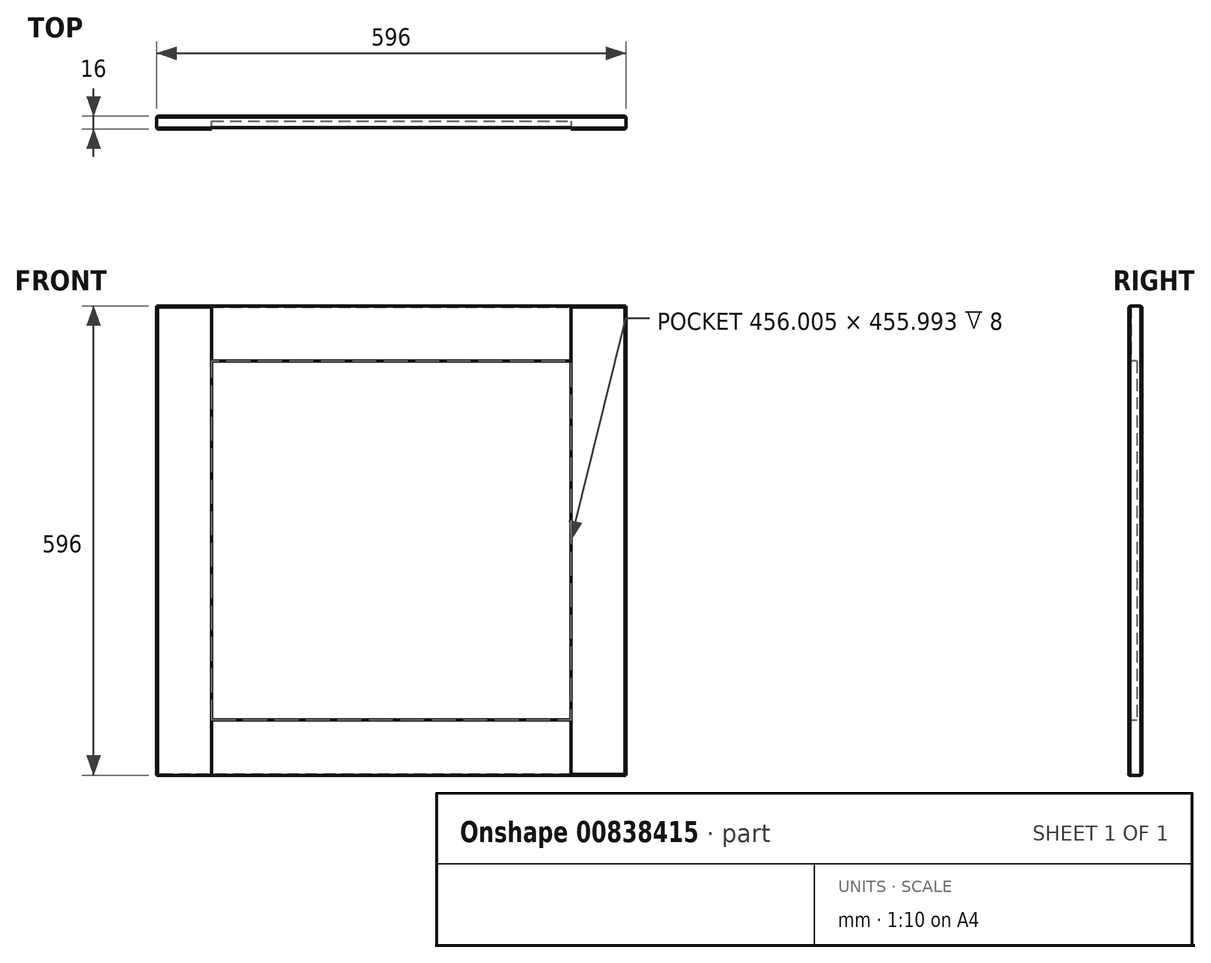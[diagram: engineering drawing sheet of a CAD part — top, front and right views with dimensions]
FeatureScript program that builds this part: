
annotation { "Feature Type Name" : "Feature", "Feature Type Description" : "" }
export const myFeature = defineFeature(function(context is Context, id is Id, definition is map)
    precondition{}
    {
        {
            var Q0;
            Q0=qCreatedBy(makeId("Front.planeOp"),FACE);
            var sketch = newSketch(context, id + "F0", { "sketchPlane" : qUnion([Q0])});
            skLineSegment(sketch, "E0.bottom", {"start": v(0, 0) * mm, "end": v(35.9, 0) * mm});
            skLineSegment(sketch, "E0.top", {"start": v(0, 30.12) * mm, "end": v(35.9, 30.12) * mm});
            skLineSegment(sketch, "E0.left", {"start": v(0, 0) * mm, "end": v(0, 30.12) * mm});
            skLineSegment(sketch, "E0.right", {"start": v(35.9, 0) * mm, "end": v(35.9, 30.12) * mm});
            skSolve(sketch);
        }
        {
            var Q0;
            Q0=makeQuery(id+"F0.imprint","IMPRINT",FACE,{"disambiguationData":[TD([[makeQuery(id+"F0.imprint","IMPRINT",EDGE,{"derivedFrom":sQuery(id+"F0.wireOp",EDGE,"E0.bottom")}),1.0]])]});
            extrude(context, id + "F1", {"entities" : qUnion([Q0]), "depth" : 16 * mm, "offsetDistance" : 25.4 * mm});
        }
        {
            var Q0;
            Q0=makeQuery(id+"F1.opExtrude","SWEPT_FACE",FACE,{"disambiguationData":[OSD([sQuery(id+"F0.wireOp",EDGE,"E0.left")])]});
            extrude(context, id + "F2", {"entities" : qUnion([Q0]), "operationType" : NewBodyOperationType.ADD, "oppositeDirection" : true, "depth" : 196 * mm, "offsetDistance" : 25 * mm});
        }
        {
            var Q0;
            {var subQ0=sQuery(id+"F0.wireOp",EDGE,"E0.bottom");Q0=makeQuery(id+"F2.boolean.opBoolean","MERGE",FACE,{"derivedFrom":[makeQuery(id+"F1.opExtrude","SWEPT_FACE",FACE,{"disambiguationData":[OSD([subQ0])]}),makeQuery(id+"F2.opExtrude","SWEPT_FACE",FACE,{"disambiguationData":[OSD([subQ0,sQuery(id+"F0.wireOp",EDGE,"E0.left")])]})]});}
            extrude(context, id + "F3", {"entities" : qUnion([Q0]), "operationType" : NewBodyOperationType.ADD, "oppositeDirection" : true, "depth" : 796 * mm, "offsetDistance" : 25 * mm});
        }
        {
            var Q0;
            {var subQ0=sQuery(id+"F0.wireOp",EDGE,"E0.left");var subQ1=sQuery(id+"F0.wireOp",EDGE,"E0.bottom");Q0=makeQuery(id+"F3.boolean.opBoolean","MERGE",FACE,{"derivedFrom":[makeQuery(id+"F2.boolean.opBoolean","MERGE",FACE,{"derivedFrom":[makeQuery(id+"F1.opExtrude","CAP_FACE",FACE,{"disambiguationData":[OSD([subQ1,sQuery(id+"F0.wireOp",EDGE,"E0.top"),subQ0,sQuery(id+"F0.wireOp",EDGE,"E0.right")])],"isStart":false}),makeQuery(id+"F2.opExtrude","SWEPT_FACE",FACE,{"disambiguationData":[OSD([subQ0]),TDD([makeQuery(id+"F1.opExtrude","CAP_EDGE",EDGE,{"disambiguationData":[OSD([subQ0])],"isStart":false})])]})]}),makeQuery(id+"F3.opExtrude","SWEPT_FACE",FACE,{"disambiguationData":[OSD([subQ1,subQ0]),TDD([makeQuery(id+"F2.boolean.opBoolean","MERGE",EDGE,{"derivedFrom":[makeQuery(id+"F1.opExtrude","CAP_EDGE",EDGE,{"disambiguationData":[OSD([subQ1])],"isStart":false}),makeQuery(id+"F2.opExtrude","SWEPT_EDGE",EDGE,{"disambiguationData":[OSD([subQ1,subQ0]),TDD([makeQuery(id+"F1.opExtrude","CAP_VERTEX",VERTEX,{"disambiguationData":[OSD([subQ1,subQ0])],"isStart":false})])]})]})])]})]});}
            var sketch = newSketch(context, id + "F4", { "sketchPlane" : qUnion([Q0])});
            skLineSegment(sketch, "E1.bottom", {"start": v(0, 796) * mm, "end": v(42.19, 796) * mm});
            skLineSegment(sketch, "E1.top", {"start": v(0, 751.57) * mm, "end": v(42.19, 751.57) * mm});
            skLineSegment(sketch, "E1.left", {"start": v(0, 796) * mm, "end": v(0, 751.57) * mm});
            skLineSegment(sketch, "E1.right", {"start": v(42.19, 796) * mm, "end": v(42.19, 751.57) * mm});
            skLineSegment(sketch, "E2.bottom", {"start": v(196, 796) * mm, "end": v(153.6, 796) * mm});
            skLineSegment(sketch, "E2.top", {"start": v(196, 746.75) * mm, "end": v(153.6, 746.75) * mm});
            skLineSegment(sketch, "E2.left", {"start": v(196, 796) * mm, "end": v(196, 746.75) * mm});
            skLineSegment(sketch, "E2.right", {"start": v(153.6, 796) * mm, "end": v(153.6, 746.75) * mm});
            skSolve(sketch);
        }
        {
            var Q0;
            Q0=makeQuery(id+"F4.imprint","IMPRINT",FACE,{"disambiguationData":[TD([[makeQuery(id+"F4.imprint","IMPRINT",EDGE,{"derivedFrom":sQuery(id+"F4.wireOp",EDGE,"E1.bottom")}),-1.0]])]});
            var Q1;
            Q1=makeQuery(id+"F4.imprint","IMPRINT",FACE,{"disambiguationData":[TD([[makeQuery(id+"F4.imprint","IMPRINT",EDGE,{"derivedFrom":sQuery(id+"F4.wireOp",EDGE,"E2.bottom")}),-1.0]])]});
            extrude(context, id + "F5", {"entities" : qUnion([Q0, Q1]), "operationType" : NewBodyOperationType.ADD, "depth" : 25 * mm, "offsetDistance" : 25 * mm});
        }
        {
            var Q0;
            {var subQ0=sQuery(id+"F0.wireOp",EDGE,"E0.left");var subQ1=sQuery(id+"F0.wireOp",EDGE,"E0.bottom");Q0=makeQuery(id+"F3.boolean.opBoolean","MERGE",FACE,{"derivedFrom":[makeQuery(id+"F2.boolean.opBoolean","MERGE",FACE,{"derivedFrom":[makeQuery(id+"F1.opExtrude","CAP_FACE",FACE,{"disambiguationData":[OSD([subQ1,sQuery(id+"F0.wireOp",EDGE,"E0.top"),subQ0,sQuery(id+"F0.wireOp",EDGE,"E0.right")])],"isStart":false}),makeQuery(id+"F2.opExtrude","SWEPT_FACE",FACE,{"disambiguationData":[OSD([subQ0]),TDD([makeQuery(id+"F1.opExtrude","CAP_EDGE",EDGE,{"disambiguationData":[OSD([subQ0])],"isStart":false})])]})]}),makeQuery(id+"F3.opExtrude","SWEPT_FACE",FACE,{"disambiguationData":[OSD([subQ1,subQ0]),TDD([makeQuery(id+"F2.boolean.opBoolean","MERGE",EDGE,{"derivedFrom":[makeQuery(id+"F1.opExtrude","CAP_EDGE",EDGE,{"disambiguationData":[OSD([subQ1])],"isStart":false}),makeQuery(id+"F2.opExtrude","SWEPT_EDGE",EDGE,{"disambiguationData":[OSD([subQ1,subQ0]),TDD([makeQuery(id+"F1.opExtrude","CAP_VERTEX",VERTEX,{"disambiguationData":[OSD([subQ1,subQ0])],"isStart":false})])]})]})])]})]});}
            var sketch = newSketch(context, id + "F6", { "sketchPlane" : qUnion([Q0])});
            skLineSegment(sketch, "E3.bottom", {"start": v(196, 0) * mm, "end": v(163.38, 0) * mm});
            skLineSegment(sketch, "E3.top", {"start": v(196, 46.55) * mm, "end": v(163.38, 46.55) * mm});
            skLineSegment(sketch, "E3.left", {"start": v(196, 0) * mm, "end": v(196, 46.55) * mm});
            skLineSegment(sketch, "E3.right", {"start": v(163.38, 0) * mm, "end": v(163.38, 46.55) * mm});
            skLineSegment(sketch, "E4.bottom", {"start": v(0, 0) * mm, "end": v(50.28, 0) * mm});
            skLineSegment(sketch, "E4.top", {"start": v(0, 44.4) * mm, "end": v(50.28, 44.4) * mm});
            skLineSegment(sketch, "E4.left", {"start": v(0, 0) * mm, "end": v(0, 44.4) * mm});
            skLineSegment(sketch, "E4.right", {"start": v(50.28, 0) * mm, "end": v(50.28, 44.4) * mm});
            skSolve(sketch);
        }
        {
            var Q0;
            Q0=makeQuery(id+"F6.imprint","IMPRINT",FACE,{"disambiguationData":[TD([[makeQuery(id+"F6.imprint","IMPRINT",EDGE,{"derivedFrom":sQuery(id+"F6.wireOp",EDGE,"E3.bottom")}),1.0]])]});
            var Q1;
            Q1=makeQuery(id+"F6.imprint","IMPRINT",FACE,{"disambiguationData":[TD([[makeQuery(id+"F6.imprint","IMPRINT",EDGE,{"derivedFrom":sQuery(id+"F6.wireOp",EDGE,"E4.bottom")}),1.0]])]});
            extrude(context, id + "F7", {"entities" : qUnion([Q0, Q1]), "operationType" : NewBodyOperationType.ADD, "depth" : 25 * mm, "offsetDistance" : 25 * mm});
        }
        {
            var Q0;
            Q0=makeQuery(id+"F7.opExtrude","SWEPT_FACE",FACE,{"disambiguationData":[OSD([sQuery(id+"F6.wireOp",EDGE,"E4.right")])]});
            extrude(context, id + "F8", {"entities" : qUnion([Q0]), "operationType" : NewBodyOperationType.ADD, "depth" : 19.72 * mm, "offsetDistance" : 25 * mm});
        }
        {
            var Q0;
            {var subQ0=sQuery(id+"F6.wireOp",EDGE,"E4.top");Q0=makeQuery(id+"F8.boolean.opBoolean","MERGE",FACE,{"derivedFrom":[makeQuery(id+"F7.opExtrude","SWEPT_FACE",FACE,{"disambiguationData":[OSD([subQ0])]}),makeQuery(id+"F8.opExtrude","SWEPT_FACE",FACE,{"disambiguationData":[OSD([subQ0,sQuery(id+"F6.wireOp",EDGE,"E4.right")])]})]});}
            extrude(context, id + "F9", {"entities" : qUnion([Q0]), "operationType" : NewBodyOperationType.ADD, "depth" : 25.6 * mm, "offsetDistance" : 25 * mm});
        }
        {
            var Q0;
            Q0=makeQuery(id+"F7.opExtrude","SWEPT_FACE",FACE,{"disambiguationData":[OSD([sQuery(id+"F6.wireOp",EDGE,"E3.right")])]});
            extrude(context, id + "F10", {"entities" : qUnion([Q0]), "operationType" : NewBodyOperationType.ADD, "depth" : 37.38 * mm, "offsetDistance" : 25 * mm});
        }
        {
            var Q0;
            {var subQ0=sQuery(id+"F6.wireOp",EDGE,"E3.top");Q0=makeQuery(id+"F10.boolean.opBoolean","MERGE",FACE,{"derivedFrom":[makeQuery(id+"F7.opExtrude","SWEPT_FACE",FACE,{"disambiguationData":[OSD([subQ0])]}),makeQuery(id+"F10.opExtrude","SWEPT_FACE",FACE,{"disambiguationData":[OSD([subQ0,sQuery(id+"F6.wireOp",EDGE,"E3.right")])]})]});}
            extrude(context, id + "F11", {"entities" : qUnion([Q0]), "operationType" : NewBodyOperationType.ADD, "depth" : 23.45 * mm, "offsetDistance" : 25 * mm});
        }
        {
            var Q0;
            Q0=makeQuery(id+"F5.opExtrude","SWEPT_FACE",FACE,{"disambiguationData":[OSD([sQuery(id+"F4.wireOp",EDGE,"E1.right")])]});
            extrude(context, id + "F12", {"entities" : qUnion([Q0]), "operationType" : NewBodyOperationType.ADD, "depth" : 27.8 * mm, "offsetDistance" : 25 * mm});
        }
        {
            var Q0;
            {var subQ0=sQuery(id+"F4.wireOp",EDGE,"E1.top");Q0=makeQuery(id+"F12.boolean.opBoolean","MERGE",FACE,{"derivedFrom":[makeQuery(id+"F5.opExtrude","SWEPT_FACE",FACE,{"disambiguationData":[OSD([subQ0])]}),makeQuery(id+"F12.opExtrude","SWEPT_FACE",FACE,{"disambiguationData":[OSD([subQ0,sQuery(id+"F4.wireOp",EDGE,"E1.right")])]})]});}
            extrude(context, id + "F13", {"entities" : qUnion([Q0]), "operationType" : NewBodyOperationType.ADD, "depth" : 25.57 * mm, "offsetDistance" : 25 * mm});
        }
        {
            var Q0;
            Q0=makeQuery(id+"F5.opExtrude","SWEPT_FACE",FACE,{"disambiguationData":[OSD([sQuery(id+"F4.wireOp",EDGE,"E2.top")])]});
            extrude(context, id + "F14", {"entities" : qUnion([Q0]), "operationType" : NewBodyOperationType.ADD, "depth" : 20.75 * mm, "offsetDistance" : 25 * mm});
        }
        {
            var Q0;
            {var subQ0=sQuery(id+"F4.wireOp",EDGE,"E2.right");Q0=makeQuery(id+"F14.boolean.opBoolean","MERGE",FACE,{"derivedFrom":[makeQuery(id+"F5.opExtrude","SWEPT_FACE",FACE,{"disambiguationData":[OSD([subQ0])]}),makeQuery(id+"F14.opExtrude","SWEPT_FACE",FACE,{"disambiguationData":[OSD([sQuery(id+"F4.wireOp",EDGE,"E2.top"),subQ0])]})]});}
            extrude(context, id + "F15", {"entities" : qUnion([Q0]), "operationType" : NewBodyOperationType.ADD, "depth" : 27.6 * mm, "offsetDistance" : 25 * mm});
        }
        {
            var Q0;
            {var subQ0=sQuery(id+"F0.wireOp",EDGE,"E0.left");var subQ1=sQuery(id+"F0.wireOp",EDGE,"E0.bottom");Q0=makeQuery(id+"F3.boolean.opBoolean","MERGE",FACE,{"derivedFrom":[makeQuery(id+"F2.boolean.opBoolean","MERGE",FACE,{"derivedFrom":[makeQuery(id+"F1.opExtrude","CAP_FACE",FACE,{"disambiguationData":[OSD([subQ1,sQuery(id+"F0.wireOp",EDGE,"E0.top"),subQ0,sQuery(id+"F0.wireOp",EDGE,"E0.right")])],"isStart":false}),makeQuery(id+"F2.opExtrude","SWEPT_FACE",FACE,{"disambiguationData":[OSD([subQ0]),TDD([makeQuery(id+"F1.opExtrude","CAP_EDGE",EDGE,{"disambiguationData":[OSD([subQ0])],"isStart":false})])]})]}),makeQuery(id+"F3.opExtrude","SWEPT_FACE",FACE,{"disambiguationData":[OSD([subQ1,subQ0]),TDD([makeQuery(id+"F2.boolean.opBoolean","MERGE",EDGE,{"derivedFrom":[makeQuery(id+"F1.opExtrude","CAP_EDGE",EDGE,{"disambiguationData":[OSD([subQ1])],"isStart":false}),makeQuery(id+"F2.opExtrude","SWEPT_EDGE",EDGE,{"disambiguationData":[OSD([subQ1,subQ0]),TDD([makeQuery(id+"F1.opExtrude","CAP_VERTEX",VERTEX,{"disambiguationData":[OSD([subQ1,subQ0])],"isStart":false})])]})]})])]})]});}
            var sketch = newSketch(context, id + "F16", { "sketchPlane" : qUnion([Q0])});
            skLineSegment(sketch, "E5.bottom", {"start": v(70, 726) * mm, "end": v(126, 726) * mm});
            skLineSegment(sketch, "E5.top", {"start": v(70, 70) * mm, "end": v(126, 70) * mm});
            skLineSegment(sketch, "E5.left", {"start": v(70, 726) * mm, "end": v(70, 70) * mm});
            skLineSegment(sketch, "E5.right", {"start": v(126, 726) * mm, "end": v(126, 70) * mm});
            skSolve(sketch);
        }
        {
            var Q0;
            Q0=makeQuery(id+"F16.imprint","IMPRINT",FACE,{"disambiguationData":[TD([[makeQuery(id+"F16.imprint","IMPRINT",EDGE,{"derivedFrom":sQuery(id+"F16.wireOp",EDGE,"E5.top")}),1.0]])]});
            extrude(context, id + "F17", {"entities" : qUnion([Q0]), "operationType" : NewBodyOperationType.REMOVE, "oppositeDirection" : true, "depth" : 10 * mm, "offsetDistance" : 25 * mm});
        }
        {
            var Q0;
            {var subQ2=sQuery(id+"F0.wireOp",EDGE,"E0.left");var subQ3=sQuery(id+"F0.wireOp",EDGE,"E0.bottom");var subQ4=makeQuery(id+"F1.opExtrude","CAP_FACE",FACE,{"disambiguationData":[OSD([subQ3,sQuery(id+"F0.wireOp",EDGE,"E0.top"),subQ2,sQuery(id+"F0.wireOp",EDGE,"E0.right")])],"isStart":false});var subQ7=makeQuery(id+"F3.opExtrude","SWEPT_FACE",FACE,{"disambiguationData":[OSD([subQ3,subQ2]),TDD([makeQuery(id+"F2.boolean.opBoolean","MERGE",EDGE,{"derivedFrom":[makeQuery(id+"F1.opExtrude","CAP_EDGE",EDGE,{"disambiguationData":[OSD([subQ3])],"isStart":false}),makeQuery(id+"F2.opExtrude","SWEPT_EDGE",EDGE,{"disambiguationData":[OSD([subQ3,subQ2]),TDD([makeQuery(id+"F1.opExtrude","CAP_VERTEX",VERTEX,{"disambiguationData":[OSD([subQ3,subQ2])],"isStart":false})])]})]})])]});var subQ8=makeQuery(id+"F2.opExtrude","SWEPT_FACE",FACE,{"disambiguationData":[OSD([subQ2]),TDD([makeQuery(id+"F1.opExtrude","CAP_EDGE",EDGE,{"disambiguationData":[OSD([subQ2])],"isStart":false})])]});Q0=makeQuery(id+"F17.boolean.opBoolean","SPLIT",FACE,{"disambiguationData":[TD([makeQuery(id+"F1.opExtrude","SWEPT_FACE",FACE,{"disambiguationData":[OSD([subQ3])]})])],"derivedFrom":makeQuery(id+"F3.boolean.opBoolean","MERGE",FACE,{"derivedFrom":[makeQuery(id+"F2.boolean.opBoolean","MERGE",FACE,{"derivedFrom":[subQ4,subQ8]}),subQ7]})});}
            var Q1;
            {var subQ2=sQuery(id+"F4.wireOp",EDGE,"E1.bottom");var subQ3=sQuery(id+"F0.wireOp",EDGE,"E0.left");var subQ4=sQuery(id+"F0.wireOp",EDGE,"E0.bottom");var subQ6=makeQuery(id+"F1.opExtrude","CAP_FACE",FACE,{"disambiguationData":[OSD([subQ4,sQuery(id+"F0.wireOp",EDGE,"E0.top"),subQ3,sQuery(id+"F0.wireOp",EDGE,"E0.right")])],"isStart":false});var subQ7=makeQuery(id+"F2.opExtrude","SWEPT_FACE",FACE,{"disambiguationData":[OSD([subQ3]),TDD([makeQuery(id+"F1.opExtrude","CAP_EDGE",EDGE,{"disambiguationData":[OSD([subQ3])],"isStart":false})])]});var subQ8=makeQuery(id+"F3.opExtrude","SWEPT_FACE",FACE,{"disambiguationData":[OSD([subQ4,subQ3]),TDD([makeQuery(id+"F2.boolean.opBoolean","MERGE",EDGE,{"derivedFrom":[makeQuery(id+"F1.opExtrude","CAP_EDGE",EDGE,{"disambiguationData":[OSD([subQ4])],"isStart":false}),makeQuery(id+"F2.opExtrude","SWEPT_EDGE",EDGE,{"disambiguationData":[OSD([subQ4,subQ3]),TDD([makeQuery(id+"F1.opExtrude","CAP_VERTEX",VERTEX,{"disambiguationData":[OSD([subQ4,subQ3])],"isStart":false})])]})]})])]});Q1=makeQuery(id+"F17.boolean.opBoolean","SPLIT",FACE,{"disambiguationData":[TD([makeQuery(id+"F5.opExtrude","SWEPT_FACE",FACE,{"disambiguationData":[OSD([subQ2])]})])],"derivedFrom":makeQuery(id+"F3.boolean.opBoolean","MERGE",FACE,{"derivedFrom":[makeQuery(id+"F2.boolean.opBoolean","MERGE",FACE,{"derivedFrom":[subQ6,subQ7]}),subQ8]})});}
            extrude(context, id + "F18", {"entities" : qUnion([Q0, Q1]), "operationType" : NewBodyOperationType.REMOVE, "oppositeDirection" : true, "depth" : 2 * mm, "offsetDistance" : 25 * mm});
        }
        {
            var Q0;
            {var subQ0=sQuery(id+"F4.wireOp",EDGE,"E1.right");var subQ1=sQuery(id+"F4.wireOp",EDGE,"E1.top");Q0=makeQuery(id+"F13.boolean.opBoolean","MERGE",FACE,{"derivedFrom":[makeQuery(id+"F12.boolean.opBoolean","MERGE",FACE,{"derivedFrom":[makeQuery(id+"F5.opExtrude","CAP_FACE",FACE,{"disambiguationData":[OSD([sQuery(id+"F4.wireOp",EDGE,"E1.bottom"),subQ1,sQuery(id+"F4.wireOp",EDGE,"E1.left"),subQ0])],"isStart":false}),makeQuery(id+"F12.opExtrude","SWEPT_FACE",FACE,{"disambiguationData":[OSD([subQ0]),TDD([makeQuery(id+"F5.opExtrude","CAP_EDGE",EDGE,{"disambiguationData":[OSD([subQ0])],"isStart":false})])]})]}),makeQuery(id+"F13.opExtrude","SWEPT_FACE",FACE,{"disambiguationData":[OSD([subQ1,subQ0]),TDD([makeQuery(id+"F12.boolean.opBoolean","MERGE",EDGE,{"derivedFrom":[makeQuery(id+"F5.opExtrude","CAP_EDGE",EDGE,{"disambiguationData":[OSD([subQ1])],"isStart":false}),makeQuery(id+"F12.opExtrude","SWEPT_EDGE",EDGE,{"disambiguationData":[OSD([subQ1,subQ0]),TDD([makeQuery(id+"F5.opExtrude","CAP_VERTEX",VERTEX,{"disambiguationData":[OSD([subQ1,subQ0])],"isStart":false})])]})]})])]})]});}
            var Q1;
            {var subQ0=sQuery(id+"F4.wireOp",EDGE,"E2.right");var subQ1=sQuery(id+"F4.wireOp",EDGE,"E2.top");Q1=makeQuery(id+"F15.boolean.opBoolean","MERGE",FACE,{"derivedFrom":[makeQuery(id+"F14.boolean.opBoolean","MERGE",FACE,{"derivedFrom":[makeQuery(id+"F5.opExtrude","CAP_FACE",FACE,{"disambiguationData":[OSD([sQuery(id+"F4.wireOp",EDGE,"E2.bottom"),subQ1,sQuery(id+"F4.wireOp",EDGE,"E2.left"),subQ0])],"isStart":false}),makeQuery(id+"F14.opExtrude","SWEPT_FACE",FACE,{"disambiguationData":[OSD([subQ1]),TDD([makeQuery(id+"F5.opExtrude","CAP_EDGE",EDGE,{"disambiguationData":[OSD([subQ1])],"isStart":false})])]})]}),makeQuery(id+"F15.opExtrude","SWEPT_FACE",FACE,{"disambiguationData":[OSD([subQ1,subQ0]),TDD([makeQuery(id+"F14.boolean.opBoolean","MERGE",EDGE,{"derivedFrom":[makeQuery(id+"F5.opExtrude","CAP_EDGE",EDGE,{"disambiguationData":[OSD([subQ0])],"isStart":false}),makeQuery(id+"F14.opExtrude","SWEPT_EDGE",EDGE,{"disambiguationData":[OSD([subQ1,subQ0]),TDD([makeQuery(id+"F5.opExtrude","CAP_VERTEX",VERTEX,{"disambiguationData":[OSD([subQ1,subQ0])],"isStart":false})])]})]})])]})]});}
            var Q2;
            {var subQ0=sQuery(id+"F6.wireOp",EDGE,"E4.right");var subQ1=sQuery(id+"F6.wireOp",EDGE,"E4.top");Q2=makeQuery(id+"F9.boolean.opBoolean","MERGE",FACE,{"derivedFrom":[makeQuery(id+"F8.boolean.opBoolean","MERGE",FACE,{"derivedFrom":[makeQuery(id+"F7.opExtrude","CAP_FACE",FACE,{"disambiguationData":[OSD([sQuery(id+"F6.wireOp",EDGE,"E4.bottom"),subQ1,sQuery(id+"F6.wireOp",EDGE,"E4.left"),subQ0])],"isStart":false}),makeQuery(id+"F8.opExtrude","SWEPT_FACE",FACE,{"disambiguationData":[OSD([subQ0]),TDD([makeQuery(id+"F7.opExtrude","CAP_EDGE",EDGE,{"disambiguationData":[OSD([subQ0])],"isStart":false})])]})]}),makeQuery(id+"F9.opExtrude","SWEPT_FACE",FACE,{"disambiguationData":[OSD([subQ1,subQ0]),TDD([makeQuery(id+"F8.boolean.opBoolean","MERGE",EDGE,{"derivedFrom":[makeQuery(id+"F7.opExtrude","CAP_EDGE",EDGE,{"disambiguationData":[OSD([subQ1])],"isStart":false}),makeQuery(id+"F8.opExtrude","SWEPT_EDGE",EDGE,{"disambiguationData":[OSD([subQ1,subQ0]),TDD([makeQuery(id+"F7.opExtrude","CAP_VERTEX",VERTEX,{"disambiguationData":[OSD([subQ1,subQ0])],"isStart":false})])]})]})])]})]});}
            var Q3;
            {var subQ0=sQuery(id+"F6.wireOp",EDGE,"E3.right");var subQ1=sQuery(id+"F6.wireOp",EDGE,"E3.top");Q3=makeQuery(id+"F11.boolean.opBoolean","MERGE",FACE,{"derivedFrom":[makeQuery(id+"F10.boolean.opBoolean","MERGE",FACE,{"derivedFrom":[makeQuery(id+"F7.opExtrude","CAP_FACE",FACE,{"disambiguationData":[OSD([sQuery(id+"F6.wireOp",EDGE,"E3.bottom"),subQ1,sQuery(id+"F6.wireOp",EDGE,"E3.left"),subQ0])],"isStart":false}),makeQuery(id+"F10.opExtrude","SWEPT_FACE",FACE,{"disambiguationData":[OSD([subQ0]),TDD([makeQuery(id+"F7.opExtrude","CAP_EDGE",EDGE,{"disambiguationData":[OSD([subQ0])],"isStart":false})])]})]}),makeQuery(id+"F11.opExtrude","SWEPT_FACE",FACE,{"disambiguationData":[OSD([subQ1,subQ0]),TDD([makeQuery(id+"F10.boolean.opBoolean","MERGE",EDGE,{"derivedFrom":[makeQuery(id+"F7.opExtrude","CAP_EDGE",EDGE,{"disambiguationData":[OSD([subQ1])],"isStart":false}),makeQuery(id+"F10.opExtrude","SWEPT_EDGE",EDGE,{"disambiguationData":[OSD([subQ1,subQ0]),TDD([makeQuery(id+"F7.opExtrude","CAP_VERTEX",VERTEX,{"disambiguationData":[OSD([subQ1,subQ0])],"isStart":false})])]})]})])]})]});}
            extrude(context, id + "F19", {"entities" : qUnion([Q0, Q1, Q2, Q3]), "operationType" : NewBodyOperationType.REMOVE, "oppositeDirection" : true, "depth" : 25 * mm, "offsetDistance" : 25 * mm});
        }
        {
            var Q0;
            {var subQ0=sQuery(id+"F4.wireOp",EDGE,"E2.left");var subQ1=sQuery(id+"F0.wireOp",EDGE,"E0.left");var subQ2=sQuery(id+"F0.wireOp",EDGE,"E0.bottom");var subQ3=sQuery(id+"F6.wireOp",EDGE,"E3.left");Q0=makeQuery(id+"F14.boolean.opBoolean","MERGE",FACE,{"derivedFrom":[makeQuery(id+"F11.boolean.opBoolean","MERGE",FACE,{"derivedFrom":[makeQuery(id+"F7.boolean.opBoolean","MERGE",FACE,{"derivedFrom":[makeQuery(id+"F5.boolean.opBoolean","MERGE",FACE,{"derivedFrom":[makeQuery(id+"F3.boolean.opBoolean","MERGE",FACE,{"derivedFrom":[makeQuery(id+"F2.opExtrude","CAP_FACE",FACE,{"disambiguationData":[OSD([subQ1])],"isStart":false}),makeQuery(id+"F3.opExtrude","SWEPT_FACE",FACE,{"disambiguationData":[OSD([subQ2,subQ1]),TDD([makeQuery(id+"F2.opExtrude","CAP_EDGE",EDGE,{"disambiguationData":[OSD([subQ2,subQ1])],"isStart":false})])]})]}),makeQuery(id+"F5.opExtrude","SWEPT_FACE",FACE,{"disambiguationData":[OSD([subQ0])]})]}),makeQuery(id+"F7.opExtrude","SWEPT_FACE",FACE,{"disambiguationData":[OSD([subQ3])]})]}),makeQuery(id+"F11.opExtrude","SWEPT_FACE",FACE,{"disambiguationData":[OSD([subQ2,subQ1,sQuery(id+"F6.wireOp",EDGE,"E3.top"),subQ3])]})]}),makeQuery(id+"F14.opExtrude","SWEPT_FACE",FACE,{"disambiguationData":[OSD([subQ2,subQ1,sQuery(id+"F4.wireOp",EDGE,"E2.top"),subQ0])]})]});}
            extrude(context, id + "F20", {"entities" : qUnion([Q0]), "operationType" : NewBodyOperationType.ADD, "depth" : 200 * mm, "offsetDistance" : 25 * mm});
        }
        {
            var Q0;
            {var subQ0=sQuery(id+"F4.wireOp",EDGE,"E2.right");var subQ1=sQuery(id+"F4.wireOp",EDGE,"E2.top");Q0=makeQuery(id+"F18.boolean.opBoolean","MERGE",FACE,{"derivedFrom":[makeQuery(id+"F15.opExtrude","CAP_FACE",FACE,{"disambiguationData":[OSD([subQ1,subQ0])],"isStart":false}),makeQuery(id+"F18.opExtrude","SWEPT_FACE",FACE,{"disambiguationData":[OSD([subQ1,subQ0])]})]});}
            var Q1;
            {var subQ0=sQuery(id+"F6.wireOp",EDGE,"E3.right");var subQ1=sQuery(id+"F6.wireOp",EDGE,"E3.top");Q1=makeQuery(id+"F18.boolean.opBoolean","MERGE",FACE,{"derivedFrom":[makeQuery(id+"F11.boolean.opBoolean","MERGE",FACE,{"derivedFrom":[makeQuery(id+"F10.opExtrude","CAP_FACE",FACE,{"disambiguationData":[OSD([subQ0])],"isStart":false}),makeQuery(id+"F11.opExtrude","SWEPT_FACE",FACE,{"disambiguationData":[OSD([subQ1,subQ0]),TDD([makeQuery(id+"F10.opExtrude","CAP_EDGE",EDGE,{"disambiguationData":[OSD([subQ1,subQ0])],"isStart":false})])]})]}),makeQuery(id+"F17.boolean.opBoolean","COPY",FACE,{"derivedFrom":makeQuery(id+"F17.opExtrude","SWEPT_FACE",FACE,{"disambiguationData":[OSD([sQuery(id+"F16.wireOp",EDGE,"E5.right")])]})}),makeQuery(id+"F18.opExtrude","SWEPT_FACE",FACE,{"disambiguationData":[OSD([subQ1,subQ0])]})]});}
            extrude(context, id + "F21", {"entities" : qUnion([Q0, Q1]), "operationType" : NewBodyOperationType.REMOVE, "oppositeDirection" : true, "depth" : 200 * mm, "offsetDistance" : 25 * mm});
        }
        {
            var Q0;
            {var subQ0=sQuery(id+"F4.wireOp",EDGE,"E2.bottom");var subQ1=sQuery(id+"F0.wireOp",EDGE,"E0.left");var subQ2=sQuery(id+"F0.wireOp",EDGE,"E0.bottom");var subQ3=sQuery(id+"F4.wireOp",EDGE,"E1.bottom");Q0=makeQuery(id+"F20.boolean.opBoolean","MERGE",FACE,{"derivedFrom":[makeQuery(id+"F15.boolean.opBoolean","MERGE",FACE,{"derivedFrom":[makeQuery(id+"F12.boolean.opBoolean","MERGE",FACE,{"derivedFrom":[makeQuery(id+"F5.boolean.opBoolean","MERGE",FACE,{"derivedFrom":[makeQuery(id+"F3.opExtrude","CAP_FACE",FACE,{"disambiguationData":[OSD([subQ2,subQ1])],"isStart":false}),makeQuery(id+"F5.opExtrude","SWEPT_FACE",FACE,{"disambiguationData":[OSD([subQ3])]}),makeQuery(id+"F5.opExtrude","SWEPT_FACE",FACE,{"disambiguationData":[OSD([subQ0])]})]}),makeQuery(id+"F12.opExtrude","SWEPT_FACE",FACE,{"disambiguationData":[OSD([subQ2,subQ1,subQ3,sQuery(id+"F4.wireOp",EDGE,"E1.right")])]})]}),makeQuery(id+"F15.opExtrude","SWEPT_FACE",FACE,{"disambiguationData":[OSD([subQ2,subQ1,subQ0,sQuery(id+"F4.wireOp",EDGE,"E2.right")])]})]}),makeQuery(id+"F20.opExtrude","SWEPT_FACE",FACE,{"disambiguationData":[OSD([subQ2,subQ1,subQ0,sQuery(id+"F4.wireOp",EDGE,"E2.left")])]})]});}
            extrude(context, id + "F22", {"entities" : qUnion([Q0]), "operationType" : NewBodyOperationType.ADD, "depth" : 200 * mm, "offsetDistance" : 25 * mm});
        }
        {
            var Q0;
            Q0=makeQuery(id+"F17.boolean.opBoolean","COPY",FACE,{"derivedFrom":makeQuery(id+"F17.opExtrude","SWEPT_FACE",FACE,{"disambiguationData":[OSD([sQuery(id+"F16.wireOp",EDGE,"E5.bottom")])]})});
            var Q1;
            {var subQ0=sQuery(id+"F16.wireOp",EDGE,"E5.right");var subQ1=sQuery(id+"F16.wireOp",EDGE,"E5.bottom");var subQ2=sQuery(id+"F4.wireOp",EDGE,"E2.right");var subQ3=sQuery(id+"F4.wireOp",EDGE,"E2.top");var subQ4=makeQuery(id+"F17.boolean.opBoolean","COPY",EDGE,{"derivedFrom":makeQuery(id+"F17.opExtrude","SWEPT_EDGE",EDGE,{"disambiguationData":[OSD([subQ3,subQ2,subQ1,subQ0])]})});Q1=makeQuery(id+"F21.boolean.opBoolean","COPY",FACE,{"derivedFrom":makeQuery(id+"F21.opExtrude","SWEPT_FACE",FACE,{"disambiguationData":[OSD([subQ3,subQ2,subQ1,subQ0]),TDD([makeQuery(id+"F18.boolean.opBoolean","MERGE",EDGE,{"derivedFrom":[subQ4,makeQuery(id+"F18.opExtrude","SWEPT_EDGE",EDGE,{"disambiguationData":[OSD([subQ3,subQ2,subQ1,subQ0])]})]}),makeQuery(id+"F18.boolean.opBoolean","SPLIT",EDGE,{"derivedFrom":subQ4})])]})});}
            extrude(context, id + "F23", {"entities" : qUnion([Q0, Q1]), "operationType" : NewBodyOperationType.REMOVE, "oppositeDirection" : true, "depth" : 200 * mm, "offsetDistance" : 25 * mm});
        }
        {
            var Q0;
            Q0=makeQuery(id+"F23.boolean.opBoolean","COPY",FACE,{"derivedFrom":makeQuery(id+"F23.opExtrude","CAP_FACE",FACE,{"disambiguationData":[OSD([sQuery(id+"F16.wireOp",EDGE,"E5.bottom")])],"isStart":false})});
            var Q1;
            Q1=makeQuery(id+"F23.boolean.opBoolean","COPY",FACE,{"derivedFrom":makeQuery(id+"F23.opExtrude","CAP_FACE",FACE,{"disambiguationData":[OSD([sQuery(id+"F4.wireOp",EDGE,"E2.top"),sQuery(id+"F4.wireOp",EDGE,"E2.right"),sQuery(id+"F16.wireOp",EDGE,"E5.bottom"),sQuery(id+"F16.wireOp",EDGE,"E5.right")])],"isStart":false})});
            extrude(context, id + "F24", {"entities" : qUnion([Q0, Q1]), "operationType" : NewBodyOperationType.ADD, "depth" : 600 * mm, "offsetDistance" : 25 * mm});
        }
        {
            var Q0;
            Q0=makeQuery(id+"F22.opExtrude","CAP_FACE",FACE,{"disambiguationData":[OSD([sQuery(id+"F0.wireOp",EDGE,"E0.bottom"),sQuery(id+"F0.wireOp",EDGE,"E0.left"),sQuery(id+"F4.wireOp",EDGE,"E1.bottom"),sQuery(id+"F4.wireOp",EDGE,"E1.right"),sQuery(id+"F4.wireOp",EDGE,"E2.bottom"),sQuery(id+"F4.wireOp",EDGE,"E2.left"),sQuery(id+"F4.wireOp",EDGE,"E2.right")])],"isStart":false});
            extrude(context, id + "F25", {"entities" : qUnion([Q0]), "operationType" : NewBodyOperationType.REMOVE, "oppositeDirection" : true, "depth" : 600 * mm, "offsetDistance" : 25 * mm, "hasDraft" : true, "draftAngle" : 3 * degree});
        }
        {
            var Q0;
            {var subQ0=sQuery(id+"F4.wireOp",EDGE,"E2.left");var subQ1=sQuery(id+"F0.wireOp",EDGE,"E0.left");var subQ2=sQuery(id+"F0.wireOp",EDGE,"E0.bottom");Q0=makeQuery(id+"F22.boolean.opBoolean","MERGE",FACE,{"derivedFrom":[makeQuery(id+"F20.opExtrude","CAP_FACE",FACE,{"disambiguationData":[OSD([subQ2,subQ1,sQuery(id+"F4.wireOp",EDGE,"E2.top"),subQ0,sQuery(id+"F6.wireOp",EDGE,"E3.top"),sQuery(id+"F6.wireOp",EDGE,"E3.left")])],"isStart":false}),makeQuery(id+"F22.opExtrude","SWEPT_FACE",FACE,{"disambiguationData":[OSD([subQ2,subQ1,sQuery(id+"F4.wireOp",EDGE,"E2.bottom"),subQ0])]})]});}
            extrude(context, id + "F26", {"entities" : qUnion([Q0]), "operationType" : NewBodyOperationType.ADD, "depth" : 200 * mm, "offsetDistance" : 25 * mm, "hasSecondDirection" : true, "secondDirectionOppositeDirection" : true, "secondDirectionDepth" : 25 * mm});
        }
        {
            var Q0;
            {var subQ0=sQuery(id+"F16.wireOp",EDGE,"E5.right");var subQ1=sQuery(id+"F16.wireOp",EDGE,"E5.bottom");var subQ2=sQuery(id+"F4.wireOp",EDGE,"E2.right");var subQ3=sQuery(id+"F4.wireOp",EDGE,"E2.top");var subQ4=makeQuery(id+"F17.boolean.opBoolean","COPY",EDGE,{"derivedFrom":makeQuery(id+"F17.opExtrude","SWEPT_EDGE",EDGE,{"disambiguationData":[OSD([subQ3,subQ2,subQ1,subQ0])]})});Q0=makeQuery(id+"F23.boolean.opBoolean","MERGE",FACE,{"derivedFrom":[makeQuery(id+"F21.boolean.opBoolean","COPY",FACE,{"derivedFrom":makeQuery(id+"F21.opExtrude","CAP_FACE",FACE,{"disambiguationData":[OSD([sQuery(id+"F6.wireOp",EDGE,"E3.top"),sQuery(id+"F6.wireOp",EDGE,"E3.right"),subQ0])],"isStart":false})}),makeQuery(id+"F23.opExtrude","SWEPT_FACE",FACE,{"disambiguationData":[OSD([subQ3,subQ2,subQ1,subQ0]),TDD([makeQuery(id+"F21.boolean.opBoolean","COPY",EDGE,{"derivedFrom":makeQuery(id+"F21.opExtrude","CAP_EDGE",EDGE,{"disambiguationData":[OSD([subQ3,subQ2,subQ1,subQ0]),TDD([makeQuery(id+"F18.boolean.opBoolean","MERGE",EDGE,{"derivedFrom":[subQ4,makeQuery(id+"F18.opExtrude","SWEPT_EDGE",EDGE,{"disambiguationData":[OSD([subQ3,subQ2,subQ1,subQ0])]})]}),makeQuery(id+"F18.boolean.opBoolean","SPLIT",EDGE,{"derivedFrom":subQ4})])],"isStart":false})})])]})]});}
            extrude(context, id + "F27", {"entities" : qUnion([Q0]), "operationType" : NewBodyOperationType.REMOVE, "oppositeDirection" : true, "depth" : 200 * mm, "offsetDistance" : 25 * mm});
        }
        {
            var Q0;
            {var subQ0=sQuery(id+"F4.wireOp",EDGE,"E2.right");var subQ1=sQuery(id+"F4.wireOp",EDGE,"E2.left");var subQ2=sQuery(id+"F4.wireOp",EDGE,"E2.bottom");var subQ3=sQuery(id+"F4.wireOp",EDGE,"E1.right");var subQ4=sQuery(id+"F4.wireOp",EDGE,"E1.bottom");var subQ5=sQuery(id+"F0.wireOp",EDGE,"E0.left");var subQ6=sQuery(id+"F0.wireOp",EDGE,"E0.bottom");Q0=makeQuery(id+"F26.boolean.opBoolean","MERGE",FACE,{"derivedFrom":[makeQuery(id+"F25.boolean.opBoolean","COPY",FACE,{"derivedFrom":makeQuery(id+"F25.opExtrude","CAP_FACE",FACE,{"disambiguationData":[OSD([subQ6,subQ5,subQ4,subQ3,subQ2,subQ1,subQ0])],"isStart":false})}),makeQuery(id+"F26.opExtrude","SWEPT_FACE",FACE,{"disambiguationData":[OSD([subQ6,subQ5,subQ4,subQ3,subQ2,sQuery(id+"F4.wireOp",EDGE,"E2.top"),subQ1,subQ0,sQuery(id+"F6.wireOp",EDGE,"E3.top"),sQuery(id+"F6.wireOp",EDGE,"E3.left")])]})]});}
            extrude(context, id + "F28", {"entities" : qUnion([Q0]), "operationType" : NewBodyOperationType.ADD, "depth" : 200 * mm, "offsetDistance" : 25 * mm});
        }
        {
            var Q0;
            {var subQ0=sQuery(id+"F16.wireOp",EDGE,"E5.right");var subQ1=sQuery(id+"F16.wireOp",EDGE,"E5.bottom");var subQ2=sQuery(id+"F4.wireOp",EDGE,"E2.right");var subQ3=sQuery(id+"F4.wireOp",EDGE,"E2.top");var subQ4=makeQuery(id+"F17.boolean.opBoolean","COPY",EDGE,{"derivedFrom":makeQuery(id+"F17.opExtrude","SWEPT_EDGE",EDGE,{"disambiguationData":[OSD([subQ3,subQ2,subQ1,subQ0])]})});Q0=makeQuery(id+"F27.boolean.opBoolean","MERGE",FACE,{"derivedFrom":[makeQuery(id+"F24.opExtrude","CAP_FACE",FACE,{"disambiguationData":[OSD([subQ3,subQ2,subQ1,subQ0])],"isStart":false}),makeQuery(id+"F27.opExtrude","SWEPT_FACE",FACE,{"disambiguationData":[OSD([subQ3,subQ2,subQ1,subQ0]),TDD([makeQuery(id+"F24.opExtrude","CAP_EDGE",EDGE,{"disambiguationData":[OSD([subQ3,subQ2,subQ1,subQ0]),TDD([makeQuery(id+"F23.boolean.opBoolean","COPY",EDGE,{"derivedFrom":makeQuery(id+"F23.opExtrude","CAP_EDGE",EDGE,{"disambiguationData":[OSD([subQ3,subQ2,subQ1,subQ0]),TDD([makeQuery(id+"F21.boolean.opBoolean","COPY",EDGE,{"derivedFrom":makeQuery(id+"F21.opExtrude","CAP_EDGE",EDGE,{"disambiguationData":[OSD([subQ3,subQ2,subQ1,subQ0]),TDD([makeQuery(id+"F18.boolean.opBoolean","MERGE",EDGE,{"derivedFrom":[subQ4,makeQuery(id+"F18.opExtrude","SWEPT_EDGE",EDGE,{"disambiguationData":[OSD([subQ3,subQ2,subQ1,subQ0])]})]}),makeQuery(id+"F18.boolean.opBoolean","SPLIT",EDGE,{"derivedFrom":subQ4})])],"isStart":false})})])],"isStart":false})})])],"isStart":false})])]})]});}
            var Q1;
            Q1=makeQuery(id+"F24.opExtrude","CAP_FACE",FACE,{"disambiguationData":[OSD([sQuery(id+"F16.wireOp",EDGE,"E5.bottom")])],"isStart":false});
            extrude(context, id + "F29", {"entities" : qUnion([Q0, Q1]), "operationType" : NewBodyOperationType.REMOVE, "oppositeDirection" : true, "depth" : 200 * mm, "offsetDistance" : 25 * mm});
        }
        {
            var Q0;
            Q0=makeQuery(id+"F28.opExtrude","CAP_EDGE",EDGE,{"disambiguationData":[OSD([sQuery(id+"F0.wireOp",EDGE,"E0.bottom"),sQuery(id+"F0.wireOp",EDGE,"E0.top"),sQuery(id+"F0.wireOp",EDGE,"E0.left"),sQuery(id+"F0.wireOp",EDGE,"E0.right"),sQuery(id+"F4.wireOp",EDGE,"E1.bottom"),sQuery(id+"F4.wireOp",EDGE,"E1.top"),sQuery(id+"F4.wireOp",EDGE,"E1.left"),sQuery(id+"F4.wireOp",EDGE,"E1.right"),sQuery(id+"F4.wireOp",EDGE,"E2.bottom"),sQuery(id+"F4.wireOp",EDGE,"E2.left"),sQuery(id+"F4.wireOp",EDGE,"E2.right"),sQuery(id+"F6.wireOp",EDGE,"E4.bottom"),sQuery(id+"F6.wireOp",EDGE,"E4.top"),sQuery(id+"F6.wireOp",EDGE,"E4.left"),sQuery(id+"F6.wireOp",EDGE,"E4.right")])],"isStart":false});
            var Q1;
            {var subQ0=sQuery(id+"F6.wireOp",EDGE,"E4.left");var subQ1=sQuery(id+"F6.wireOp",EDGE,"E4.top");var subQ2=sQuery(id+"F4.wireOp",EDGE,"E1.left");var subQ3=sQuery(id+"F4.wireOp",EDGE,"E1.top");var subQ4=sQuery(id+"F4.wireOp",EDGE,"E1.bottom");var subQ5=sQuery(id+"F0.wireOp",EDGE,"E0.left");var subQ6=sQuery(id+"F0.wireOp",EDGE,"E0.bottom");Q1=makeQuery(id+"F28.boolean.opBoolean","MERGE",EDGE,{"derivedFrom":[makeQuery(id+"F22.boolean.opBoolean","MERGE",EDGE,{"derivedFrom":[makeQuery(id+"F19.boolean.opBoolean","MERGE",EDGE,{"derivedFrom":[makeQuery(id+"F3.boolean.opBoolean","MERGE",EDGE,{"derivedFrom":[makeQuery(id+"F1.opExtrude","CAP_EDGE",EDGE,{"disambiguationData":[OSD([subQ5])],"isStart":false}),makeQuery(id+"F3.opExtrude","SWEPT_EDGE",EDGE,{"disambiguationData":[OSD([subQ6,subQ5]),TDD([makeQuery(id+"F1.opExtrude","CAP_VERTEX",VERTEX,{"disambiguationData":[OSD([subQ6,subQ5])],"isStart":false})])]})]}),makeQuery(id+"F19.opExtrude","CAP_EDGE",EDGE,{"disambiguationData":[OSD([subQ6,subQ5,subQ1,subQ0])],"isStart":false}),makeQuery(id+"F19.opExtrude","CAP_EDGE",EDGE,{"disambiguationData":[OSD([subQ6,subQ5,subQ3,subQ2])],"isStart":false})]}),makeQuery(id+"F22.opExtrude","SWEPT_EDGE",EDGE,{"disambiguationData":[OSD([subQ4,subQ2])]})]}),makeQuery(id+"F28.opExtrude","SWEPT_EDGE",EDGE,{"disambiguationData":[OSD([subQ6,sQuery(id+"F0.wireOp",EDGE,"E0.top"),subQ5,sQuery(id+"F0.wireOp",EDGE,"E0.right"),subQ4,subQ3,subQ2,sQuery(id+"F4.wireOp",EDGE,"E1.right"),sQuery(id+"F4.wireOp",EDGE,"E2.bottom"),sQuery(id+"F4.wireOp",EDGE,"E2.left"),sQuery(id+"F4.wireOp",EDGE,"E2.right"),sQuery(id+"F6.wireOp",EDGE,"E4.bottom"),subQ1,subQ0,sQuery(id+"F6.wireOp",EDGE,"E4.right")])]})]});}
            var Q2;
            Q2=makeQuery(id+"F28.opExtrude","CAP_EDGE",EDGE,{"disambiguationData":[OSD([sQuery(id+"F0.wireOp",EDGE,"E0.bottom"),sQuery(id+"F0.wireOp",EDGE,"E0.top"),sQuery(id+"F0.wireOp",EDGE,"E0.left"),sQuery(id+"F0.wireOp",EDGE,"E0.right"),sQuery(id+"F4.wireOp",EDGE,"E1.bottom"),sQuery(id+"F4.wireOp",EDGE,"E1.right"),sQuery(id+"F4.wireOp",EDGE,"E2.bottom"),sQuery(id+"F4.wireOp",EDGE,"E2.top"),sQuery(id+"F4.wireOp",EDGE,"E2.left"),sQuery(id+"F4.wireOp",EDGE,"E2.right"),sQuery(id+"F6.wireOp",EDGE,"E3.bottom"),sQuery(id+"F6.wireOp",EDGE,"E3.top"),sQuery(id+"F6.wireOp",EDGE,"E3.left"),sQuery(id+"F6.wireOp",EDGE,"E3.right")])],"isStart":false});
            var Q3;
            {var subQ0=sQuery(id+"F6.wireOp",EDGE,"E3.left");var subQ1=sQuery(id+"F6.wireOp",EDGE,"E3.top");var subQ2=sQuery(id+"F4.wireOp",EDGE,"E2.left");var subQ3=sQuery(id+"F4.wireOp",EDGE,"E2.top");var subQ4=sQuery(id+"F4.wireOp",EDGE,"E2.bottom");var subQ5=sQuery(id+"F0.wireOp",EDGE,"E0.left");var subQ6=sQuery(id+"F0.wireOp",EDGE,"E0.bottom");Q3=makeQuery(id+"F28.boolean.opBoolean","MERGE",EDGE,{"derivedFrom":[makeQuery(id+"F26.opExtrude","CAP_EDGE",EDGE,{"disambiguationData":[OSD([subQ6,subQ5,subQ4,subQ3,subQ2,subQ1,subQ0])],"isStart":false}),makeQuery(id+"F28.opExtrude","SWEPT_EDGE",EDGE,{"disambiguationData":[OSD([subQ6,sQuery(id+"F0.wireOp",EDGE,"E0.top"),subQ5,sQuery(id+"F0.wireOp",EDGE,"E0.right"),sQuery(id+"F4.wireOp",EDGE,"E1.bottom"),sQuery(id+"F4.wireOp",EDGE,"E1.right"),subQ4,subQ3,subQ2,sQuery(id+"F4.wireOp",EDGE,"E2.right"),sQuery(id+"F6.wireOp",EDGE,"E3.bottom"),subQ1,subQ0,sQuery(id+"F6.wireOp",EDGE,"E3.right")])]})]});}
            var Q4;
            {var subQ0=sQuery(id+"F6.wireOp",EDGE,"E3.left");var subQ1=sQuery(id+"F6.wireOp",EDGE,"E3.bottom");Q4=makeQuery(id+"F26.boolean.opBoolean","MERGE",EDGE,{"derivedFrom":[makeQuery(id+"F20.boolean.opBoolean","MERGE",EDGE,{"derivedFrom":[makeQuery(id+"F19.boolean.opBoolean","COPY",EDGE,{"derivedFrom":makeQuery(id+"F19.opExtrude","CAP_EDGE",EDGE,{"disambiguationData":[OSD([sQuery(id+"F0.wireOp",EDGE,"E0.bottom"),sQuery(id+"F0.wireOp",EDGE,"E0.left"),subQ1,sQuery(id+"F6.wireOp",EDGE,"E3.right")])],"isStart":false})}),makeQuery(id+"F20.opExtrude","SWEPT_EDGE",EDGE,{"disambiguationData":[OSD([subQ1,subQ0])]})]}),makeQuery(id+"F26.opExtrude","SWEPT_EDGE",EDGE,{"disambiguationData":[OSD([subQ1,subQ0])]})]});}
            var Q5;
            Q5=makeQuery(id+"F19.boolean.opBoolean","COPY",EDGE,{"derivedFrom":makeQuery(id+"F19.opExtrude","CAP_EDGE",EDGE,{"disambiguationData":[OSD([sQuery(id+"F0.wireOp",EDGE,"E0.bottom"),sQuery(id+"F0.wireOp",EDGE,"E0.left"),sQuery(id+"F6.wireOp",EDGE,"E4.bottom"),sQuery(id+"F6.wireOp",EDGE,"E4.right")])],"isStart":false})});
            var Q6;
            {var subQ0=sQuery(id+"F0.wireOp",EDGE,"E0.right");var subQ1=sQuery(id+"F0.wireOp",EDGE,"E0.left");var subQ2=sQuery(id+"F0.wireOp",EDGE,"E0.top");var subQ3=sQuery(id+"F0.wireOp",EDGE,"E0.bottom");Q6=makeQuery(id+"F28.boolean.opBoolean","MERGE",FACE,{"derivedFrom":[makeQuery(id+"F26.boolean.opBoolean","MERGE",FACE,{"derivedFrom":[makeQuery(id+"F22.boolean.opBoolean","MERGE",FACE,{"derivedFrom":[makeQuery(id+"F20.boolean.opBoolean","MERGE",FACE,{"derivedFrom":[makeQuery(id+"F3.boolean.opBoolean","MERGE",FACE,{"derivedFrom":[makeQuery(id+"F2.boolean.opBoolean","MERGE",FACE,{"derivedFrom":[makeQuery(id+"F1.opExtrude","CAP_FACE",FACE,{"disambiguationData":[OSD([subQ3,subQ2,subQ1,subQ0])],"isStart":true}),makeQuery(id+"F2.opExtrude","SWEPT_FACE",FACE,{"disambiguationData":[OSD([subQ1]),TDD([makeQuery(id+"F1.opExtrude","CAP_EDGE",EDGE,{"disambiguationData":[OSD([subQ1])],"isStart":true})])]})]}),makeQuery(id+"F3.opExtrude","SWEPT_FACE",FACE,{"disambiguationData":[OSD([subQ3,subQ1]),TDD([makeQuery(id+"F2.boolean.opBoolean","MERGE",EDGE,{"derivedFrom":[makeQuery(id+"F1.opExtrude","CAP_EDGE",EDGE,{"disambiguationData":[OSD([subQ3])],"isStart":true}),makeQuery(id+"F2.opExtrude","SWEPT_EDGE",EDGE,{"disambiguationData":[OSD([subQ3,subQ1]),TDD([makeQuery(id+"F1.opExtrude","CAP_VERTEX",VERTEX,{"disambiguationData":[OSD([subQ3,subQ1])],"isStart":true})])]})]})])]})]}),makeQuery(id+"F20.opExtrude","SWEPT_FACE",FACE,{"disambiguationData":[OSD([subQ3,subQ1])]})]}),makeQuery(id+"F22.opExtrude","SWEPT_FACE",FACE,{"disambiguationData":[OSD([subQ3,subQ1])]})]}),makeQuery(id+"F26.opExtrude","SWEPT_FACE",FACE,{"disambiguationData":[OSD([subQ3,subQ1])]})]}),makeQuery(id+"F28.opExtrude","SWEPT_FACE",FACE,{"disambiguationData":[OSD([subQ3,subQ2,subQ1,subQ0,sQuery(id+"F4.wireOp",EDGE,"E1.bottom"),sQuery(id+"F4.wireOp",EDGE,"E1.right"),sQuery(id+"F4.wireOp",EDGE,"E2.bottom"),sQuery(id+"F4.wireOp",EDGE,"E2.top"),sQuery(id+"F4.wireOp",EDGE,"E2.left"),sQuery(id+"F4.wireOp",EDGE,"E2.right"),sQuery(id+"F6.wireOp",EDGE,"E3.top"),sQuery(id+"F6.wireOp",EDGE,"E3.left")])]})]});}
            chamfer(context, id + "F30", {"entities" : qUnion([Q0, Q1, Q2, Q3, Q4, Q5, Q6]), "width" : 1 * mm, "tangentPropagation" : true});
        }
    });
